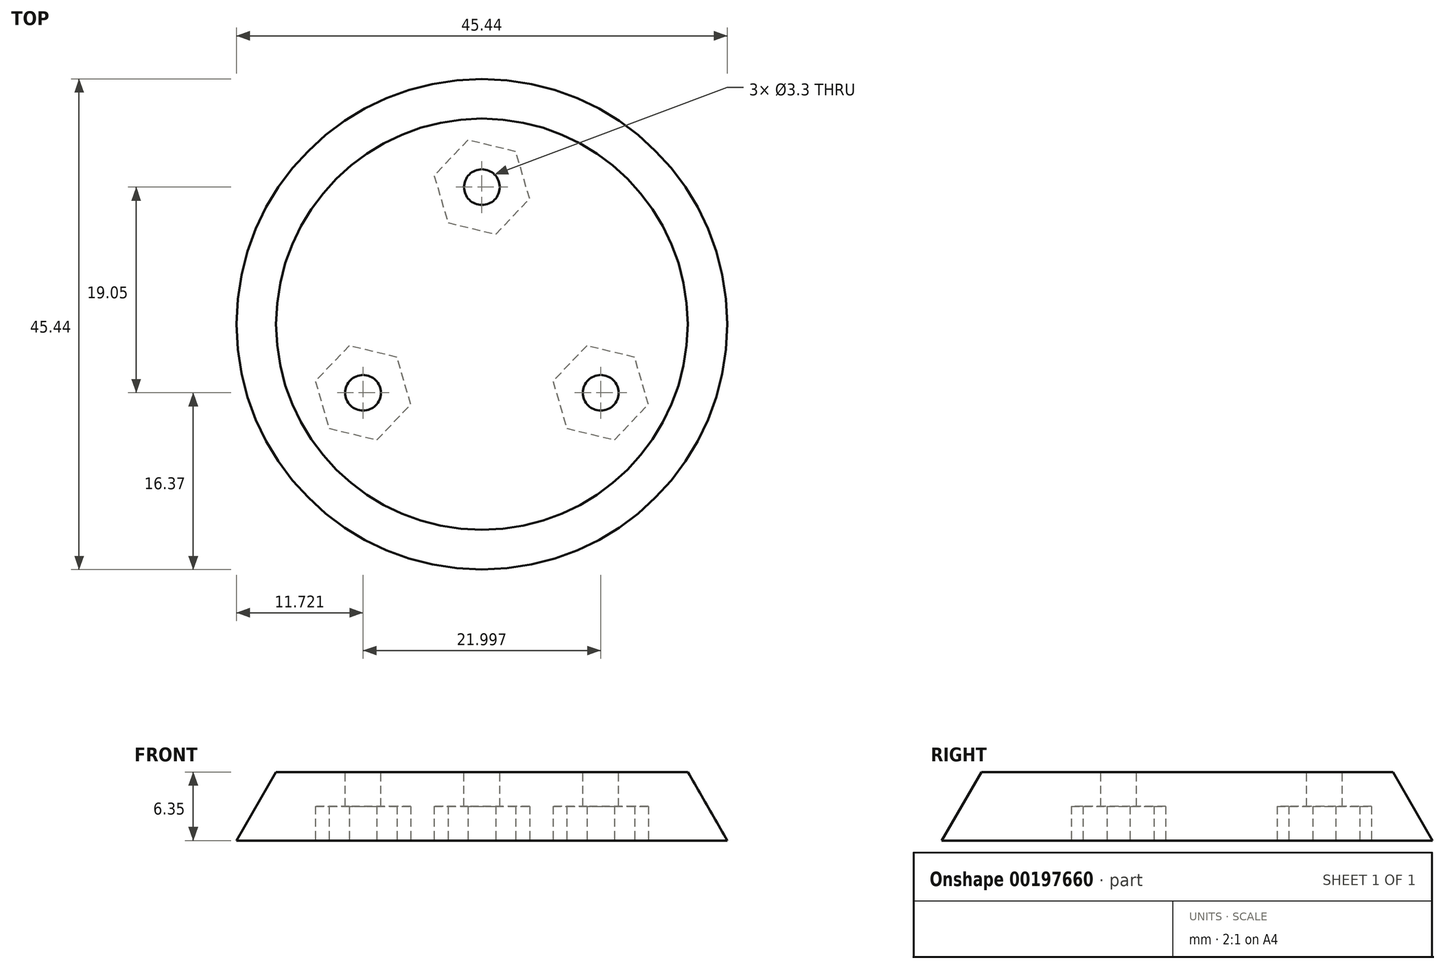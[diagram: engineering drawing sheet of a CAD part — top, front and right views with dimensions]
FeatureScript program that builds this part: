
annotation { "Feature Type Name" : "Feature", "Feature Type Description" : "" }
export const myFeature = defineFeature(function(context is Context, id is Id, definition is map)
    precondition{}
    {
        {
            var Q0;
            Q0=qCreatedBy(makeId("Top.planeOp"),FACE);
            var sketch = newSketch(context, id + "F0", { "sketchPlane" : qUnion([Q0])});
            skCircle(sketch, "E0", {"center": v(0, 0) * mm, "radius": 19.05 * mm});
            skSolve(sketch);
        }
        {
            var Q0;
            Q0 = qSketchRegion(id + "F0", true);
            extrude(context, id + "F1", {"entities" : qUnion([Q0]), "oppositeDirection" : true, "depth" : 6.35 * mm, "hasDraft" : true, "draftAngle" : 30 * degree});
        }
        {
            var Q0;
            Q0=makeQuery(id+"F1.opExtrude","CAP_FACE",FACE,{"disambiguationData":[OSD([sQuery(id+"F0.wireOp",EDGE,"E0")])],"isStart":true});
            var sketch = newSketch(context, id + "F2", { "sketchPlane" : qUnion([Q0])});
            skCircle(sketch, "E1", {"center": v(0, 0) * mm, "radius": 12.7 * mm, "construction": true});
            skCircle(sketch, "E2", {"center": v(0, 12.7) * mm, "radius": 1.65 * mm});
            skCircle(sketch, "E3.1.0", {"center": v(-11, -6.35) * mm, "radius": 1.65 * mm});
            skCircle(sketch, "E3.2.0", {"center": v(11, -6.35) * mm, "radius": 1.65 * mm});
            skSolve(sketch);
        }
        {
            var Q0;
            Q0 = qSketchRegion(id + "F2", true);
            extrude(context, id + "F3", {"entities" : qUnion([Q0]), "operationType" : NewBodyOperationType.REMOVE, "oppositeDirection" : true, "depth" : 25.4 * mm});
        }
        {
            var Q0;
            Q0=makeQuery(id+"F1.opExtrude","CAP_FACE",FACE,{"disambiguationData":[OSD([sQuery(id+"F0.wireOp",EDGE,"E0")])],"isStart":false});
            var sketch = newSketch(context, id + "F4", { "sketchPlane" : qUnion([Q0])});
            skCircle(sketch, "E4.cCircle", {"center": v(0, -12.7) * mm, "radius": 3.94 * mm, "construction": true});
            skLineSegment(sketch, "E4.0", {"start": v(1.28, -8.34) * mm, "end": v(4.42, -11.62) * mm});
            skLineSegment(sketch, "E4.1", {"start": v(4.42, -11.62) * mm, "end": v(3.14, -15.99) * mm});
            skLineSegment(sketch, "E4.2", {"start": v(3.14, -15.99) * mm, "end": v(-1.28, -17.06) * mm});
            skLineSegment(sketch, "E4.3", {"start": v(-1.28, -17.06) * mm, "end": v(-4.42, -13.78) * mm});
            skLineSegment(sketch, "E4.4", {"start": v(-4.42, -13.78) * mm, "end": v(-3.14, -9.41) * mm});
            skLineSegment(sketch, "E4.5", {"start": v(-3.14, -9.41) * mm, "end": v(1.28, -8.34) * mm});
            skPoint(sketch, "E4.0.midPoint", {"position": v(2.85, -9.98) * mm});
            skCircle(sketch, "E5.1.0", {"center": v(11, 6.35) * mm, "radius": 3.94 * mm, "construction": true});
            skLineSegment(sketch, "E5.1.1", {"start": v(14.14, 3.06) * mm, "end": v(9.72, 1.99) * mm});
            skLineSegment(sketch, "E5.1.2", {"start": v(9.72, 1.99) * mm, "end": v(6.58, 5.27) * mm});
            skLineSegment(sketch, "E5.1.3", {"start": v(6.58, 5.27) * mm, "end": v(7.86, 9.64) * mm});
            skLineSegment(sketch, "E5.1.4", {"start": v(7.86, 9.64) * mm, "end": v(12.28, 10.71) * mm});
            skLineSegment(sketch, "E5.1.5", {"start": v(12.28, 10.71) * mm, "end": v(15.42, 7.43) * mm});
            skLineSegment(sketch, "E5.1.6", {"start": v(15.42, 7.43) * mm, "end": v(14.14, 3.06) * mm});
            skCircle(sketch, "E5.2.0", {"center": v(-11, 6.35) * mm, "radius": 3.94 * mm, "construction": true});
            skLineSegment(sketch, "E5.2.1", {"start": v(-9.72, 10.71) * mm, "end": v(-6.58, 7.43) * mm});
            skLineSegment(sketch, "E5.2.2", {"start": v(-6.58, 7.43) * mm, "end": v(-7.86, 3.06) * mm});
            skLineSegment(sketch, "E5.2.3", {"start": v(-7.86, 3.06) * mm, "end": v(-12.28, 1.99) * mm});
            skLineSegment(sketch, "E5.2.4", {"start": v(-12.28, 1.99) * mm, "end": v(-15.42, 5.27) * mm});
            skLineSegment(sketch, "E5.2.5", {"start": v(-15.42, 5.27) * mm, "end": v(-14.14, 9.64) * mm});
            skLineSegment(sketch, "E5.2.6", {"start": v(-14.14, 9.64) * mm, "end": v(-9.72, 10.71) * mm});
            skPoint(sketch, "E5.center", {"position": v(0, 0) * mm});
            skSolve(sketch);
        }
        {
            var Q0;
            Q0 = qSketchRegion(id + "F4", true);
            extrude(context, id + "F5", {"entities" : qUnion([Q0]), "operationType" : NewBodyOperationType.REMOVE, "oppositeDirection" : true, "depth" : 3.17 * mm});
        }
    });
